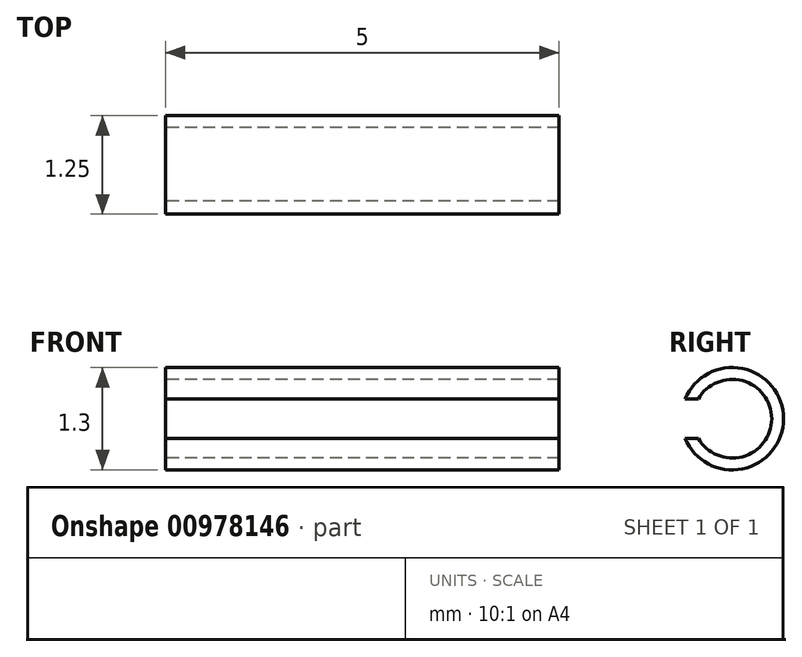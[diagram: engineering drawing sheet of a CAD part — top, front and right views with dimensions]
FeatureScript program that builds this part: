
annotation { "Feature Type Name" : "Feature", "Feature Type Description" : "" }
export const myFeature = defineFeature(function(context is Context, id is Id, definition is map)
    precondition{}
    {
        {
            var Q0;
            Q0=qCreatedBy(makeId("Front.planeOp"),FACE);
            var sketch = newSketch(context, id + "F0", { "sketchPlane" : qUnion([Q0])});
            skLineSegment(sketch, "E0", {"start": v(-2.97, 0) * mm, "end": v(3.45, 0) * mm, "construction": true});
            skLineSegment(sketch, "E1", {"start": v(-1.75, 0.65) * mm, "end": v(3.25, 0.65) * mm});
            skLineSegment(sketch, "E2", {"start": v(3.25, 0.65) * mm, "end": v(3.25, 0.5) * mm});
            skLineSegment(sketch, "E3", {"start": v(3.25, 0.5) * mm, "end": v(-1.75, 0.5) * mm});
            skLineSegment(sketch, "E4", {"start": v(-1.75, 0.5) * mm, "end": v(-1.75, 0.65) * mm});
            skSolve(sketch);
        }
        {
            var Q0;
            Q0 = qSketchRegion(id + "F0", true);
            var Q1;
            Q1=sQuery(id+"F0.wireOp",EDGE,"E0");
            revolve(context, id + "F1", {"surfaceOperationType" : NewSurfaceOperationType.NEW, "entities" : qUnion([Q0]), "axis" : qUnion([Q1]), "revolveType" : RevolveType.FULL});
        }
        {
            var Q0;
            Q0=qCreatedBy(makeId("Front.planeOp"),FACE);
            var sketch = newSketch(context, id + "F2", { "sketchPlane" : qUnion([Q0])});
            skLineSegment(sketch, "E5.bottom", {"start": v(5.3, 0.25) * mm, "end": v(-5.3, 0.25) * mm});
            skLineSegment(sketch, "E5.top", {"start": v(5.3, -0.25) * mm, "end": v(-5.3, -0.25) * mm});
            skLineSegment(sketch, "E5.left", {"start": v(5.3, 0.25) * mm, "end": v(5.3, -0.25) * mm});
            skLineSegment(sketch, "E5.right", {"start": v(-5.3, 0.25) * mm, "end": v(-5.3, -0.25) * mm});
            skPoint(sketch, "E5.middle", {"position": v(0, 0) * mm});
            skSolve(sketch);
        }
        {
            var Q0;
            Q0 = qSketchRegion(id + "F2", true);
            extrude(context, id + "F3", {"entities" : qUnion([Q0]), "operationType" : NewBodyOperationType.REMOVE, "depth" : 25 * mm, "offsetDistance" : 25 * mm});
        }
    });
